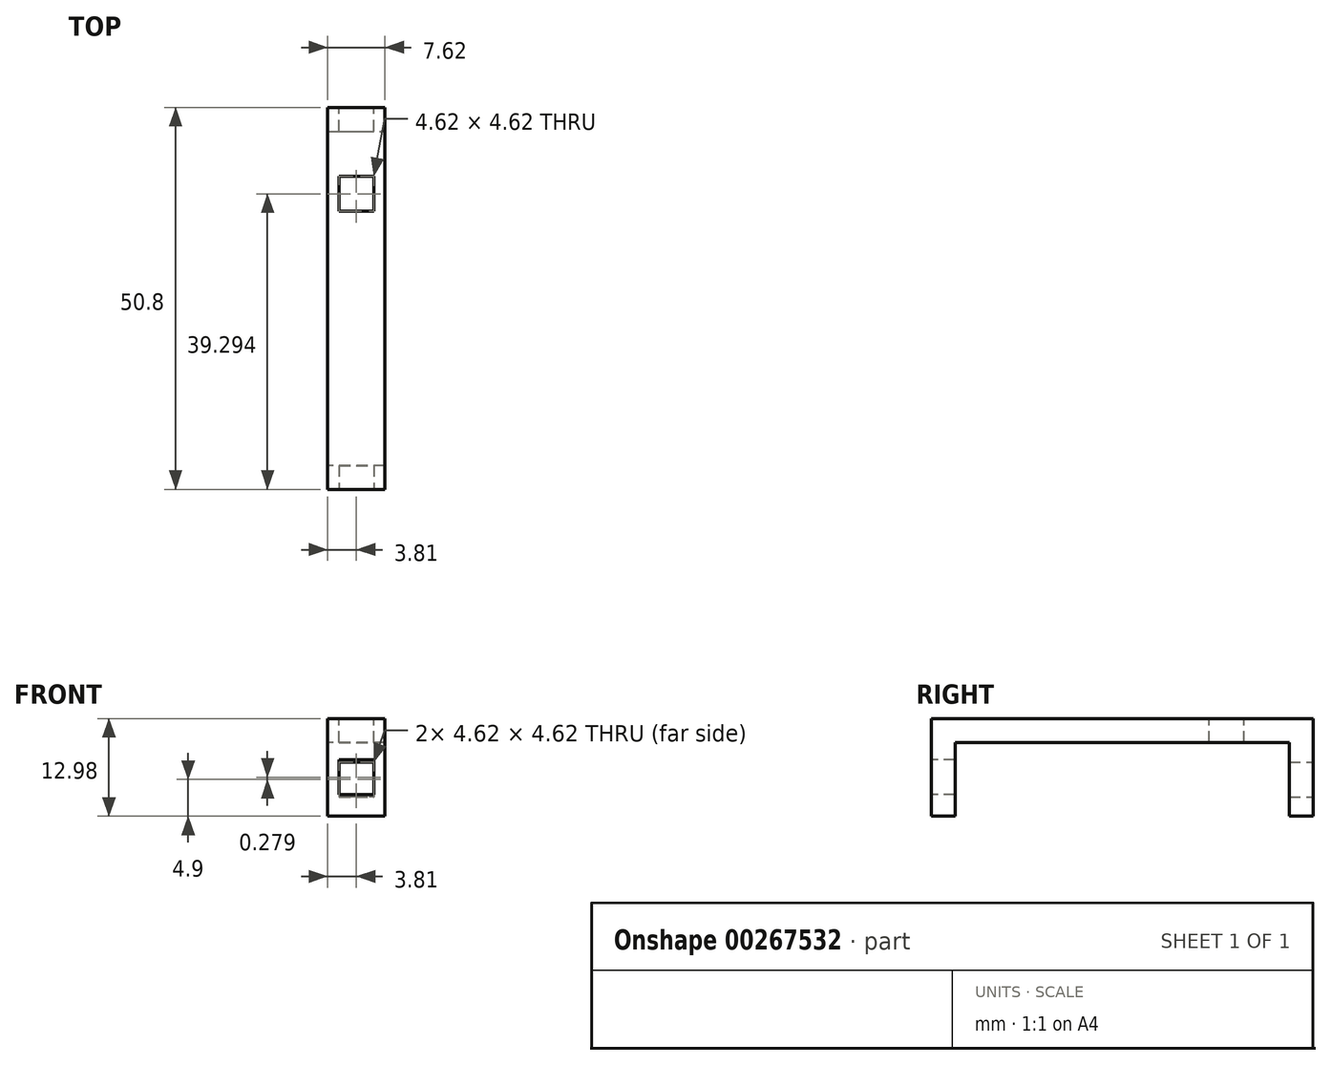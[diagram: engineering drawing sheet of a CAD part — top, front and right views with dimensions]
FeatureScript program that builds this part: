
annotation { "Feature Type Name" : "Feature", "Feature Type Description" : "" }
export const myFeature = defineFeature(function(context is Context, id is Id, definition is map)
    precondition{}
    {
        {
            var Q0;
            Q0=qCreatedBy(makeId("Front.planeOp"),FACE);
            var sketch = newSketch(context, id + "F0", { "sketchPlane" : qUnion([Q0])});
            skLineSegment(sketch, "E0.bottom", {"start": v(-2.31, 2.31) * mm, "end": v(2.31, 2.31) * mm});
            skLineSegment(sketch, "E0.top", {"start": v(-2.31, -2.31) * mm, "end": v(2.31, -2.31) * mm});
            skLineSegment(sketch, "E0.left", {"start": v(-2.31, 2.31) * mm, "end": v(-2.31, -2.31) * mm});
            skLineSegment(sketch, "E0.right", {"start": v(2.31, 2.31) * mm, "end": v(2.31, -2.31) * mm});
            skPoint(sketch, "E0.middle", {"position": v(0, 0) * mm});
            skLineSegment(sketch, "E1.bottom", {"start": v(-3.8, 4.9) * mm, "end": v(3.8, 4.9) * mm});
            skLineSegment(sketch, "E1.top", {"start": v(-3.8, -4.9) * mm, "end": v(3.81, -4.9) * mm});
            skLineSegment(sketch, "E1.left", {"start": v(-3.8, 4.9) * mm, "end": v(-3.8, -4.9) * mm});
            skLineSegment(sketch, "E1.right", {"start": v(3.8, 4.9) * mm, "end": v(3.81, -4.9) * mm});
            skLineSegment(sketch, "E2", {"start": v(-3.8, 4.9) * mm, "end": v(-3.8, 8.08) * mm});
            skLineSegment(sketch, "E3", {"start": v(3.81, 4.9) * mm, "end": v(3.81, 8.08) * mm});
            skLineSegment(sketch, "E4", {"start": v(3.81, 8.08) * mm, "end": v(-3.8, 8.08) * mm});
            skSolve(sketch);
        }
        {
            var Q0;
            Q0=makeQuery(id+"F0.imprint","IMPRINT",FACE,{"disambiguationData":[TD([[makeQuery(id+"F0.imprint","IMPRINT",EDGE,{"derivedFrom":sQuery(id+"F0.wireOp",EDGE,"E1.bottom")}),1.0]])]});
            extrude(context, id + "F1", {"entities" : qUnion([Q0]), "depth" : 50.8 * mm});
        }
        {
            var Q0;
            Q0=makeQuery(id+"F0.imprint","IMPRINT",FACE,{"disambiguationData":[TD([[makeQuery(id+"F0.imprint","IMPRINT",EDGE,{"derivedFrom":sQuery(id+"F0.wireOp",EDGE,"E0.bottom")}),1.0]])]});
            extrude(context, id + "F2", {"entities" : qUnion([Q0]), "operationType" : NewBodyOperationType.ADD, "depth" : 3.17 * mm});
        }
        {
            var Q0;
            Q0=makeQuery(id+"F1.opExtrude","SWEPT_FACE",FACE,{"disambiguationData":[OSD([sQuery(id+"F0.wireOp",EDGE,"E1.bottom")])]});
            var sketch = newSketch(context, id + "F3", { "sketchPlane" : qUnion([Q0])});
            skLineSegment(sketch, "E5", {"start": v(3.8, 50.8) * mm, "end": v(3.8, 47.63) * mm});
            skLineSegment(sketch, "E6", {"start": v(3.8, 47.63) * mm, "end": v(-3.8, 47.63) * mm});
            skLineSegment(sketch, "E7", {"start": v(-3.8, 47.63) * mm, "end": v(-3.8, 50.8) * mm});
            skLineSegment(sketch, "E8", {"start": v(-3.8, 50.8) * mm, "end": v(3.8, 50.8) * mm});
            skSolve(sketch);
        }
        {
            var Q0;
            Q0=makeQuery(id+"F3.imprint","IMPRINT",FACE,{"disambiguationData":[TD([[makeQuery(id+"F3.imprint","IMPRINT",EDGE,{"derivedFrom":sQuery(id+"F3.wireOp",EDGE,"E5")}),-1.0]])]});
            extrude(context, id + "F4", {"entities" : qUnion([Q0]), "operationType" : NewBodyOperationType.ADD, "depth" : 9.8 * mm});
        }
        {
            var Q0;
            Q0=makeQuery(id+"F4.boolean.opBoolean","MERGE",FACE,{"derivedFrom":[makeQuery(id+"F1.opExtrude","CAP_FACE",FACE,{"disambiguationData":[OSD([sQuery(id+"F0.wireOp",EDGE,"E1.bottom"),sQuery(id+"F0.wireOp",EDGE,"E2"),sQuery(id+"F0.wireOp",EDGE,"E3"),sQuery(id+"F0.wireOp",EDGE,"E4")])],"isStart":false}),makeQuery(id+"F4.opExtrude","SWEPT_FACE",FACE,{"disambiguationData":[OSD([sQuery(id+"F3.wireOp",EDGE,"E8")])]})]});
            var sketch = newSketch(context, id + "F5", { "sketchPlane" : qUnion([Q0])});
            skPoint(sketch, "E9.endSnap0", {"position": v(0, -4.9) * mm});
            skLineSegment(sketch, "E10", {"start": v(3.81, 1.59) * mm, "end": v(2.31, 1.59) * mm});
            skPoint(sketch, "E10.endSnap0", {"position": v(3.81, 1.59) * mm});
            skLineSegment(sketch, "E11", {"start": v(2.31, 1.59) * mm, "end": v(2.31, 2.6) * mm});
            skLineSegment(sketch, "E12", {"start": v(2.31, 2.6) * mm, "end": v(-2.31, 2.6) * mm});
            skLineSegment(sketch, "E13", {"start": v(-2.31, 2.6) * mm, "end": v(-2.31, -2.03) * mm});
            skLineSegment(sketch, "E14", {"start": v(-2.31, -2.03) * mm, "end": v(2.31, -2.03) * mm});
            skLineSegment(sketch, "E15", {"start": v(2.31, -2.03) * mm, "end": v(2.31, 2.6) * mm});
            skSolve(sketch);
        }
        {
            var Q0;
            {var subQ3=sQuery(id+"F5.wireOp",EDGE,"E12");Q0=makeQuery(id+"F5.imprint","IMPRINT",FACE,{"disambiguationData":[TD([[makeQuery(id+"F5.imprint","IMPRINT",EDGE,{"derivedFrom":subQ3}),1.0]])]});}
            extrude(context, id + "F6", {"entities" : qUnion([Q0]), "operationType" : NewBodyOperationType.REMOVE, "oppositeDirection" : true, "depth" : 25.4 * mm});
        }
        {
            var Q0;
            Q0=makeQuery(id+"F1.opExtrude","SWEPT_FACE",FACE,{"disambiguationData":[OSD([sQuery(id+"F0.wireOp",EDGE,"E4")])]});
            var sketch = newSketch(context, id + "F7", { "sketchPlane" : qUnion([Q0])});
            skLineSegment(sketch, "E16", {"start": v(0, 0) * mm, "end": v(0, -9.2) * mm});
            skLineSegment(sketch, "E17", {"start": v(0, -9.2) * mm, "end": v(-2.31, -9.2) * mm});
            skLineSegment(sketch, "E18", {"start": v(0, -9.2) * mm, "end": v(2.31, -9.2) * mm});
            skLineSegment(sketch, "E19", {"start": v(2.31, -9.2) * mm, "end": v(2.31, -13.82) * mm});
            skLineSegment(sketch, "E20", {"start": v(-2.31, -9.2) * mm, "end": v(-2.31, -13.82) * mm});
            skLineSegment(sketch, "E21", {"start": v(-2.31, -13.82) * mm, "end": v(2.31, -13.82) * mm});
            skSolve(sketch);
        }
        {
            var Q0;
            Q0=makeQuery(id+"F7.imprint","IMPRINT",FACE,{"disambiguationData":[TD([[makeQuery(id+"F7.imprint","IMPRINT",EDGE,{"derivedFrom":sQuery(id+"F7.wireOp",EDGE,"E17")}),1.0]])]});
            extrude(context, id + "F8", {"entities" : qUnion([Q0]), "operationType" : NewBodyOperationType.REMOVE, "oppositeDirection" : true, "depth" : 25.4 * mm});
        }
    });
